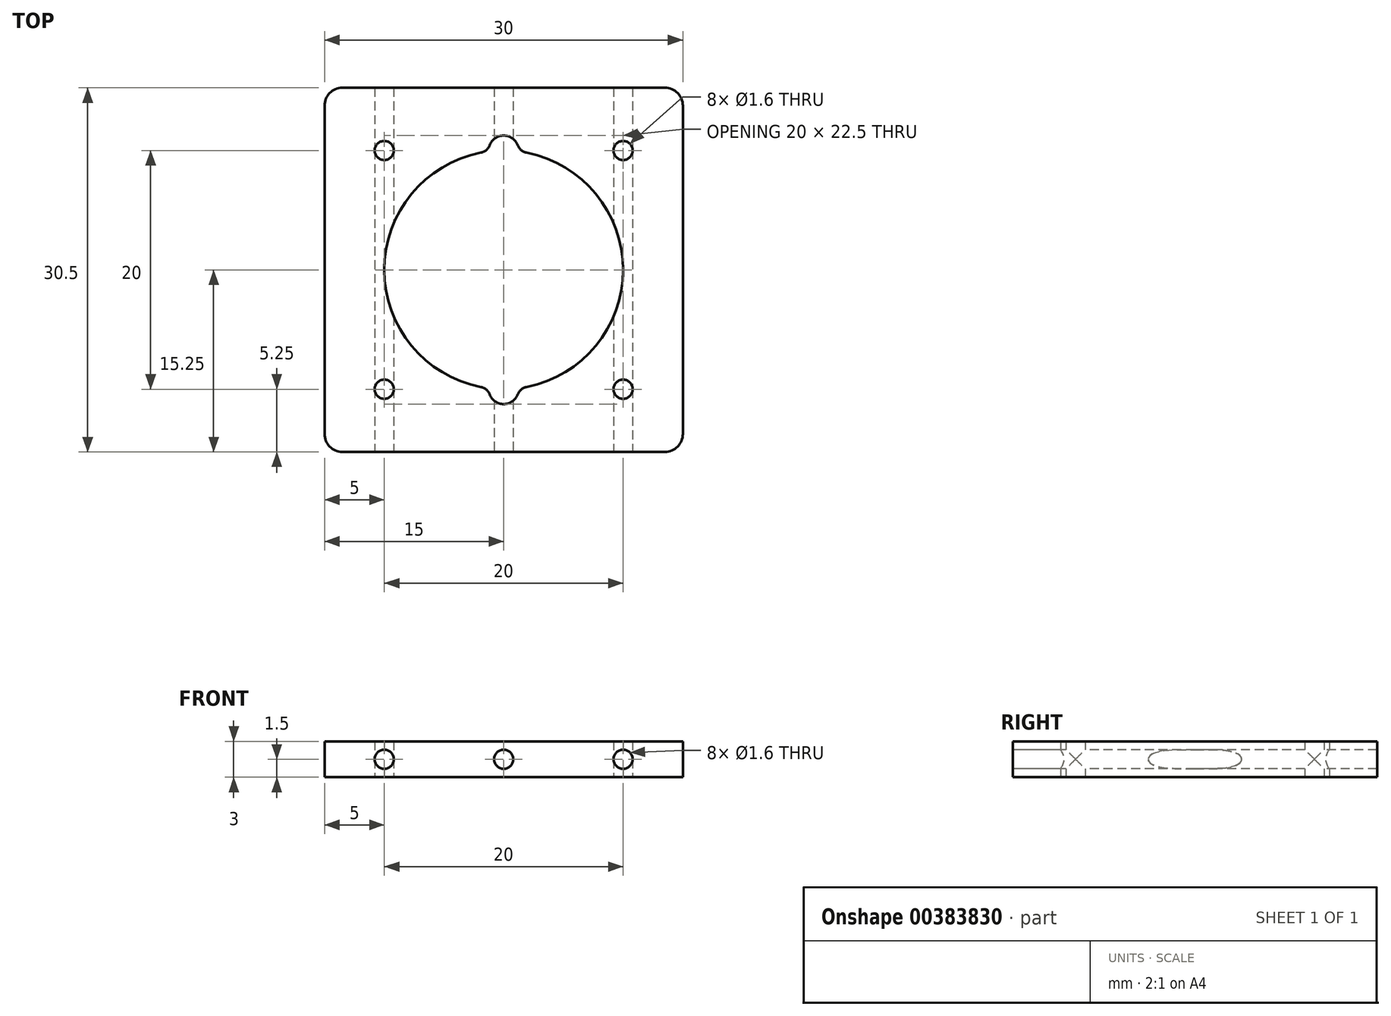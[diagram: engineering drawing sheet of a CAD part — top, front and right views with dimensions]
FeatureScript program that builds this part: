
annotation { "Feature Type Name" : "Feature", "Feature Type Description" : "" }
export const myFeature = defineFeature(function(context is Context, id is Id, definition is map)
    precondition{}
    {
        {
            var Q0;
            Q0=qCreatedBy(makeId("Top.planeOp"),FACE);
            var sketch = newSketch(context, id + "F0", { "sketchPlane" : qUnion([Q0])});
            skLineSegment(sketch, "E0.bottom", {"start": v(-13.5, 15.25) * mm, "end": v(13.5, 15.25) * mm});
            skLineSegment(sketch, "E0.top", {"start": v(-13.5, -15.25) * mm, "end": v(13.5, -15.25) * mm});
            skLineSegment(sketch, "E0.left", {"start": v(-15, 13.75) * mm, "end": v(-15, -13.75) * mm});
            skLineSegment(sketch, "E0.right", {"start": v(15, 13.75) * mm, "end": v(15, -13.75) * mm});
            skPoint(sketch, "E0.middle", {"position": v(0, 0) * mm});
            skLineSegment(sketch, "E1.bottom", {"start": v(-10, 10) * mm, "end": v(10, 10) * mm, "construction": true});
            skLineSegment(sketch, "E1.top", {"start": v(-10, -10) * mm, "end": v(10, -10) * mm, "construction": true});
            skLineSegment(sketch, "E1.left", {"start": v(-10, 10) * mm, "end": v(-10, -10) * mm, "construction": true});
            skLineSegment(sketch, "E1.right", {"start": v(10, 10) * mm, "end": v(10, -10) * mm, "construction": true});
            skCircle(sketch, "E2", {"center": v(-10, 10) * mm, "radius": 0.8 * mm});
            skCircle(sketch, "E3.1.0", {"center": v(-10, -10) * mm, "radius": 0.8 * mm});
            skCircle(sketch, "E3.2.0", {"center": v(10, -10) * mm, "radius": 0.8 * mm});
            skCircle(sketch, "E4.1.3.0", {"center": v(10, 10) * mm, "radius": 0.8 * mm});
            skLineSegment(sketch, "E5", {"start": v(0, 15.25) * mm, "end": v(0, 10) * mm, "construction": true});
            skLineSegment(sketch, "E6", {"start": v(-10, 15.25) * mm, "end": v(-10, 10) * mm, "construction": true});
            skPoint(sketch, "E7.visualSharp", {"position": v(-15, 15.25) * mm});
            skArc(sketch, "E7.filletArc", {"start": v(-13.5, 15.25) * mm, "mid": v(-14.56, 14.81) * mm, "end": v(-15, 13.75) * mm});
            skPoint(sketch, "E8.visualSharp", {"position": v(15, 15.25) * mm});
            skArc(sketch, "E8.filletArc", {"start": v(15, 13.75) * mm, "mid": v(14.56, 14.81) * mm, "end": v(13.5, 15.25) * mm});
            skPoint(sketch, "E9.visualSharp", {"position": v(15, -15.25) * mm});
            skArc(sketch, "E9.filletArc", {"start": v(13.5, -15.25) * mm, "mid": v(14.56, -14.81) * mm, "end": v(15, -13.75) * mm});
            skPoint(sketch, "E10.visualSharp", {"position": v(-15, -15.25) * mm});
            skArc(sketch, "E10.filletArc", {"start": v(-15, -13.75) * mm, "mid": v(-14.56, -14.81) * mm, "end": v(-13.5, -15.25) * mm});
            skPoint(sketch, "E11", {"position": v(-10, 10.8) * mm});
            skCircle(sketch, "E12", {"center": v(0, 0) * mm, "radius": 10 * mm});
            skArc(sketch, "E13", {"start": v(1.25, 10) * mm, "mid": v(0, 11.25) * mm, "end": v(-1.25, 10) * mm});
            skLineSegment(sketch, "E14", {"start": v(-1.25, 10) * mm, "end": v(-1.25, 9.92) * mm});
            skLineSegment(sketch, "E15.MirrorCS", {"start": v(1.25, 10) * mm, "end": v(1.25, 9.92) * mm});
            skLineSegment(sketch, "E16.MirrorCS", {"start": v(-1.25, -10) * mm, "end": v(-1.25, -9.92) * mm});
            skLineSegment(sketch, "E17.MirrorCS", {"start": v(1.25, -10) * mm, "end": v(1.25, -9.92) * mm});
            skArc(sketch, "E18.MirrorCS", {"start": v(1.25, -10) * mm, "mid": v(0, -11.25) * mm, "end": v(-1.25, -10) * mm});
            skSolve(sketch);
        }
        {
            var Q0;
            Q0 = qSketchRegion(id + "F0", true);
            extrude(context, id + "F1", {"entities" : qUnion([Q0]), "depth" : 3 * mm, "offsetDistance" : 25 * mm});
        }
        {
            var Q0;
            Q0=makeQuery(id+"F1.opExtrude","SWEPT_FACE",FACE,{"disambiguationData":[OSD([sQuery(id+"F0.wireOp",EDGE,"E0.top")])]});
            var sketch = newSketch(context, id + "F2", { "sketchPlane" : qUnion([Q0])});
            skLineSegment(sketch, "E19", {"start": v(0, 3) * mm, "end": v(0, 0) * mm, "construction": true});
            skCircle(sketch, "E20", {"center": v(0, 1.5) * mm, "radius": 0.8 * mm});
            skCircle(sketch, "E21", {"center": v(10, 1.5) * mm, "radius": 0.8 * mm});
            skCircle(sketch, "E22.MirrorC", {"center": v(-10, 1.5) * mm, "radius": 0.8 * mm});
            skSolve(sketch);
        }
        {
            var Q0;
            Q0 = qSketchRegion(id + "F2", true);
            extrude(context, id + "F3", {"entities" : qUnion([Q0]), "operationType" : NewBodyOperationType.REMOVE, "endBound" : BoundingType.THROUGH_ALL, "oppositeDirection" : true, "depth" : 25 * mm, "offsetDistance" : 25 * mm});
        }
        {
            var Q0;
            Q0=makeQuery(id+"F1.opExtrude","SWEPT_EDGE",EDGE,{"disambiguationData":[OSD([sQuery(id+"F0.wireOp",EDGE,"E12"),sQuery(id+"F0.wireOp",EDGE,"E15.MirrorCS")])]});
            var Q1;
            Q1=makeQuery(id+"F1.opExtrude","SWEPT_EDGE",EDGE,{"disambiguationData":[OSD([sQuery(id+"F0.wireOp",EDGE,"E12"),sQuery(id+"F0.wireOp",EDGE,"E14")])]});
            var Q2;
            Q2=makeQuery(id+"F1.opExtrude","SWEPT_EDGE",EDGE,{"disambiguationData":[OSD([sQuery(id+"F0.wireOp",EDGE,"E12"),sQuery(id+"F0.wireOp",EDGE,"E16.MirrorCS")])]});
            var Q3;
            Q3=makeQuery(id+"F1.opExtrude","SWEPT_EDGE",EDGE,{"disambiguationData":[OSD([sQuery(id+"F0.wireOp",EDGE,"E12"),sQuery(id+"F0.wireOp",EDGE,"E17.MirrorCS")])]});
            fillet(context, id + "F4", {"entities" : qUnion([Q0, Q1, Q2, Q3]), "radius" : 1 * mm, "tangentPropagation" : true, "allowEdgeOverflow" : false});
        }
    });
